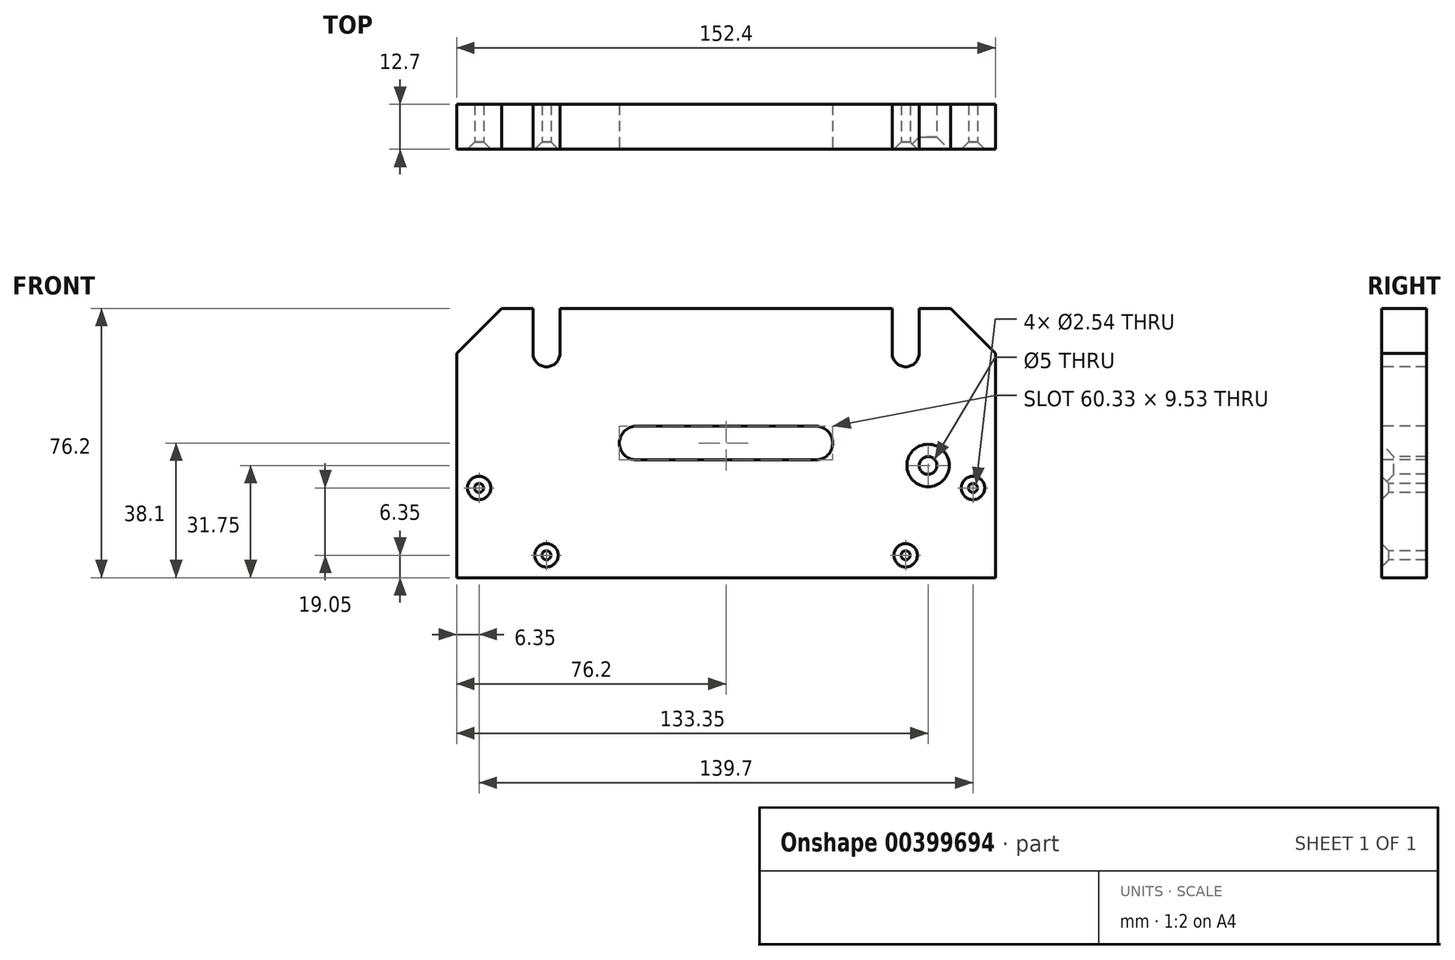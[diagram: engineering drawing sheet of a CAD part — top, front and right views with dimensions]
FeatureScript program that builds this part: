
annotation { "Feature Type Name" : "Feature", "Feature Type Description" : "" }
export const myFeature = defineFeature(function(context is Context, id is Id, definition is map)
    precondition{}
    {
        {
            var Q0;
            Q0=qCreatedBy(makeId("Front.planeOp"),FACE);
            var sketch = newSketch(context, id + "F0", { "sketchPlane" : qUnion([Q0])});
            skLineSegment(sketch, "E0.bottom", {"start": v(-76.2, 38.1) * mm, "end": v(76.2, 38.1) * mm});
            skLineSegment(sketch, "E0.top", {"start": v(-76.2, -38.1) * mm, "end": v(76.2, -38.1) * mm});
            skLineSegment(sketch, "E0.left", {"start": v(-76.2, 38.1) * mm, "end": v(-76.2, -38.1) * mm});
            skLineSegment(sketch, "E0.right", {"start": v(76.2, 38.1) * mm, "end": v(76.2, -38.1) * mm});
            skLineSegment(sketch, "E1", {"start": v(-76.2, 25.4) * mm, "end": v(-63.5, 38.1) * mm});
            skLineSegment(sketch, "E2", {"start": v(0, 38.1) * mm, "end": v(0, -38.1) * mm, "construction": true});
            skLineSegment(sketch, "E3.MirrorCS", {"start": v(76.2, 25.4) * mm, "end": v(63.5, 38.1) * mm});
            skSolve(sketch);
        }
        {
            var Q0;
            {var subQ1=sQuery(id+"F0.wireOp",EDGE,"E0.top");Q0=makeQuery(id+"F0.imprint","IMPRINT",FACE,{"disambiguationData":[TD([[makeQuery(id+"F0.imprint","IMPRINT",EDGE,{"derivedFrom":subQ1}),1.0]])]});}
            extrude(context, id + "F1", {"entities" : qUnion([Q0]), "depth" : 12.7 * mm});
        }
        {
            var Q0;
            Q0=makeQuery(id+"F1.opExtrude","CAP_FACE",FACE,{"disambiguationData":[OSD([sQuery(id+"F0.wireOp",EDGE,"E0.bottom"),sQuery(id+"F0.wireOp",EDGE,"E0.top"),sQuery(id+"F0.wireOp",EDGE,"E0.left"),sQuery(id+"F0.wireOp",EDGE,"E0.right"),sQuery(id+"F0.wireOp",EDGE,"E1"),sQuery(id+"F0.wireOp",EDGE,"E3.MirrorCS")])],"isStart":false});
            var sketch = newSketch(context, id + "F2", { "sketchPlane" : qUnion([Q0])});
            skLineSegment(sketch, "E4", {"start": v(0, 38.1) * mm, "end": v(0, -38.1) * mm, "construction": true});
            skLineSegment(sketch, "E5", {"start": v(-54.6, 38.1) * mm, "end": v(-54.6, 25.4) * mm});
            skLineSegment(sketch, "E6", {"start": v(-50.8, 38.1) * mm, "end": v(-50.8, 14.68) * mm, "construction": true});
            skArc(sketch, "E7", {"start": v(-54.6, 25.4) * mm, "mid": v(-50.8, 21.59) * mm, "end": v(-46.99, 25.4) * mm});
            skLineSegment(sketch, "E8.MirrorCS", {"start": v(-46.99, 38.1) * mm, "end": v(-46.99, 25.4) * mm});
            skLineSegment(sketch, "E9.MirrorCS", {"start": v(54.61, 38.1) * mm, "end": v(54.61, 25.4) * mm});
            skLineSegment(sketch, "E10.MirrorCS", {"start": v(47, 38.1) * mm, "end": v(47, 25.4) * mm});
            skArc(sketch, "E11.MirrorCS", {"start": v(54.61, 25.4) * mm, "mid": v(50.8, 21.59) * mm, "end": v(47, 25.4) * mm});
            skLineSegment(sketch, "E12", {"start": v(-34.63, 0) * mm, "end": v(53.06, 0) * mm, "construction": true});
            skLineSegment(sketch, "E13", {"start": v(0, 4.76) * mm, "end": v(-25.4, 4.76) * mm});
            skArc(sketch, "E14", {"start": v(-25.4, 4.76) * mm, "mid": v(-30.16, 0) * mm, "end": v(-25.4, -4.76) * mm});
            skLineSegment(sketch, "E15.MirrorCS", {"start": v(0, -4.76) * mm, "end": v(-25.4, -4.76) * mm});
            skLineSegment(sketch, "E16.MirrorCS", {"start": v(0, -4.76) * mm, "end": v(25.4, -4.76) * mm});
            skArc(sketch, "E17.MirrorCS", {"start": v(25.4, 4.76) * mm, "mid": v(30.16, 0) * mm, "end": v(25.4, -4.76) * mm});
            skLineSegment(sketch, "E18.MirrorCS", {"start": v(0, 4.76) * mm, "end": v(25.4, 4.76) * mm});
            skSolve(sketch);
        }
        {
            var Q0;
            {var subQ0=sQuery(id+"F2.wireOp",EDGE,"E5");Q0=makeQuery(id+"F2.imprint","IMPRINT",FACE,{"disambiguationData":[TD([[makeQuery(id+"F2.imprint","IMPRINT",EDGE,{"derivedFrom":subQ0}),1.0]])]});}
            var Q1;
            Q1=makeQuery(id+"F2.imprint","IMPRINT",FACE,{"disambiguationData":[TD([[makeQuery(id+"F2.imprint","IMPRINT",EDGE,{"derivedFrom":sQuery(id+"F2.wireOp",EDGE,"E13")}),1.0]])]});
            var Q2;
            {var subQ0=sQuery(id+"F2.wireOp",EDGE,"E9.MirrorCS");Q2=makeQuery(id+"F2.imprint","IMPRINT",FACE,{"disambiguationData":[TD([[makeQuery(id+"F2.imprint","IMPRINT",EDGE,{"derivedFrom":subQ0}),-1.0]])]});}
            extrude(context, id + "F3", {"entities" : qUnion([Q0, Q1, Q2]), "operationType" : NewBodyOperationType.REMOVE, "endBound" : BoundingType.THROUGH_ALL, "oppositeDirection" : true, "depth" : 25.4 * mm});
        }
        {
            var Q0;
            Q0=makeQuery(id+"F1.opExtrude","CAP_FACE",FACE,{"disambiguationData":[OSD([sQuery(id+"F0.wireOp",EDGE,"E0.bottom"),sQuery(id+"F0.wireOp",EDGE,"E0.top"),sQuery(id+"F0.wireOp",EDGE,"E0.left"),sQuery(id+"F0.wireOp",EDGE,"E0.right"),sQuery(id+"F0.wireOp",EDGE,"E1"),sQuery(id+"F0.wireOp",EDGE,"E3.MirrorCS")])],"isStart":false});
            var sketch = newSketch(context, id + "F4", { "sketchPlane" : qUnion([Q0])});
            skLineSegment(sketch, "E19", {"start": v(0, 38.1) * mm, "end": v(0, -38.1) * mm, "construction": true});
            skLineSegment(sketch, "E20", {"start": v(-76.2, -31.75) * mm, "end": v(76.2, -31.75) * mm, "construction": true});
            skLineSegment(sketch, "E21", {"start": v(-69.85, 17.06) * mm, "end": v(-69.85, -38.1) * mm, "construction": true});
            skPoint(sketch, "E22", {"position": v(-50.8, -31.75) * mm});
            skPoint(sketch, "E23", {"position": v(-69.85, -12.7) * mm});
            skPoint(sketch, "E24.MirrorP", {"position": v(50.8, -31.75) * mm});
            skPoint(sketch, "E25.MirrorP", {"position": v(69.85, -12.7) * mm});
            skPoint(sketch, "E26", {"position": v(57.15, -6.35) * mm});
            skSolve(sketch);
        }
        {
            var Q0;
            Q0=sQuery(id+"F4.wireOp",VERTEX,"E23");
            var Q1;
            Q1=sQuery(id+"F4.wireOp",VERTEX,"E22");
            var Q2;
            Q2=sQuery(id+"F4.wireOp",VERTEX,"E24.MirrorP");
            var Q3;
            Q3=sQuery(id+"F4.wireOp",VERTEX,"E25.MirrorP");
            var Q4;
            Q4=makeQuery(id+"F1.opExtrude","SWEPT_BODY",BODY,{"disambiguationData":[OSD([sQuery(id+"F0.wireOp",EDGE,"E0.bottom"),sQuery(id+"F0.wireOp",EDGE,"E0.top"),sQuery(id+"F0.wireOp",EDGE,"E0.left"),sQuery(id+"F0.wireOp",EDGE,"E0.right"),sQuery(id+"F0.wireOp",EDGE,"E1"),sQuery(id+"F0.wireOp",EDGE,"E3.MirrorCS")])]});
            hole(context, id + "F5", {"style" : HoleStyle.C_SINK, "endStyle" : HoleEndStyle.THROUGH, "holeDiameter" : 2.54 * mm, "cSinkDiameter" : 6.6 * mm, "cSinkAngle" : 90 * degree, "isTappedThrough" : true, "tappedDepth" : 12.7 * mm, "tapClearance" : 3, "locations" : qUnion([Q0, Q1, Q2, Q3]), "scope" : qUnion([Q4])});
        }
        {
            var Q0;
            Q0=sQuery(id+"F4.wireOp",VERTEX,"E26");
            var Q1;
            Q1=makeQuery(id+"F1.opExtrude","SWEPT_BODY",BODY,{"disambiguationData":[OSD([sQuery(id+"F0.wireOp",EDGE,"E0.bottom"),sQuery(id+"F0.wireOp",EDGE,"E0.top"),sQuery(id+"F0.wireOp",EDGE,"E0.left"),sQuery(id+"F0.wireOp",EDGE,"E0.right"),sQuery(id+"F0.wireOp",EDGE,"E1"),sQuery(id+"F0.wireOp",EDGE,"E3.MirrorCS")])]});
            hole(context, id + "F6", {"style" : HoleStyle.C_SINK, "endStyle" : HoleEndStyle.THROUGH, "holeDiameter" : 5 * mm, "cSinkDiameter" : 12 * mm, "cSinkAngle" : 90 * degree, "isTappedThrough" : true, "tappedDepth" : 12.7 * mm, "tapClearance" : 3, "locations" : qUnion([Q0]), "scope" : qUnion([Q1])});
        }
    });
